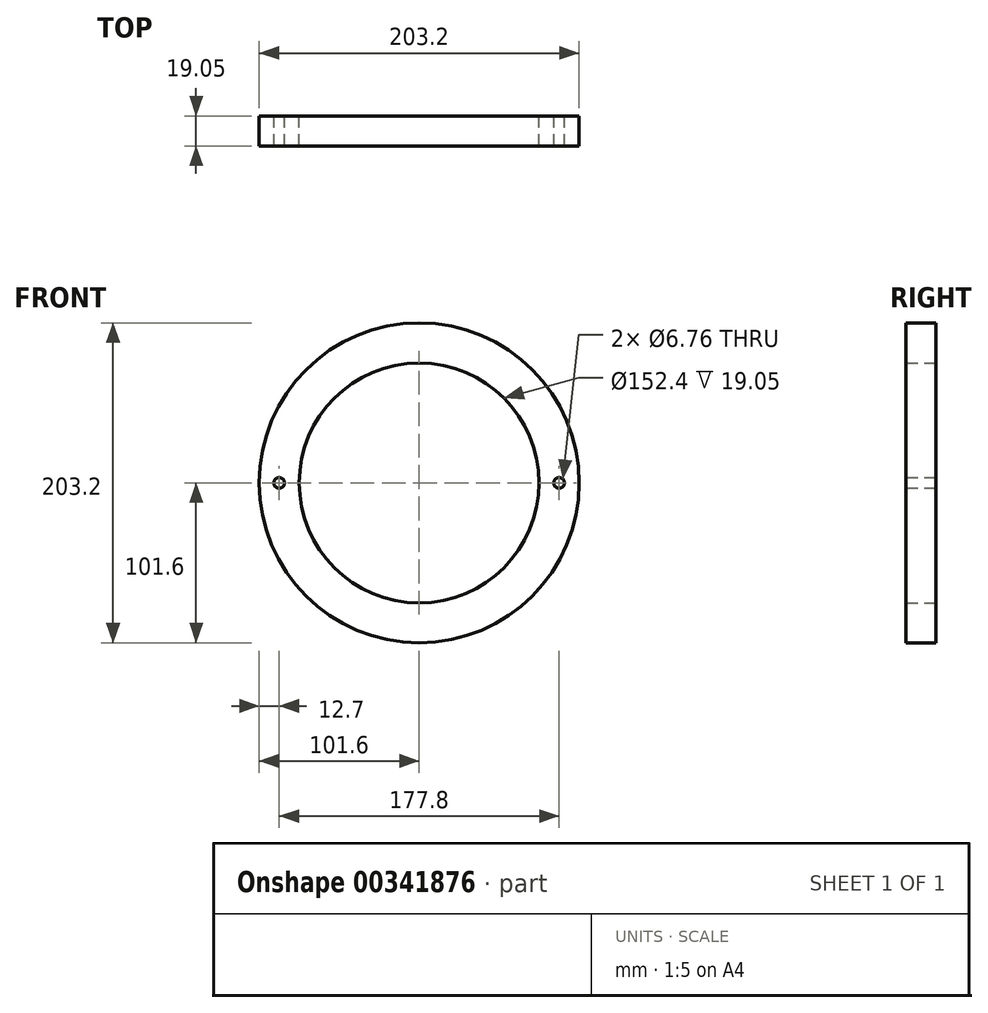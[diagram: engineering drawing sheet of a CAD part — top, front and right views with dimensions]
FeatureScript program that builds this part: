
annotation { "Feature Type Name" : "Feature", "Feature Type Description" : "" }
export const myFeature = defineFeature(function(context is Context, id is Id, definition is map)
    precondition{}
    {
        {
            var Q0;
            Q0=qCreatedBy(makeId("Front.planeOp"),FACE);
            var sketch = newSketch(context, id + "F0", { "sketchPlane" : qUnion([Q0])});
            skCircle(sketch, "E0", {"center": v(0, 0) * mm, "radius": 101.6 * mm});
            skCircle(sketch, "E1.0", {"center": v(0, 0) * mm, "radius": 76.2 * mm});
            skSolve(sketch);
        }
        {
            var Q0;
            Q0 = qSketchRegion(id + "F0", true);
            extrude(context, id + "F1", {"entities" : qUnion([Q0]), "depth" : 19.05 * mm});
        }
        {
            var Q0;
            Q0=makeQuery(id+"F1.opExtrude","CAP_FACE",FACE,{"disambiguationData":[OSD([sQuery(id+"F0.wireOp",EDGE,"E0"),sQuery(id+"F0.wireOp",EDGE,"E1.0")])],"isStart":false});
            var sketch = newSketch(context, id + "F2", { "sketchPlane" : qUnion([Q0])});
            skLineSegment(sketch, "E2", {"start": v(-101.6, 0) * mm, "end": v(-76.2, 0) * mm});
            skLineSegment(sketch, "E3", {"start": v(76.2, 0) * mm, "end": v(101.6, 0) * mm});
            skPoint(sketch, "E4", {"position": v(-88.9, 0) * mm});
            skPoint(sketch, "E5", {"position": v(88.9, 0) * mm});
            skSolve(sketch);
        }
        {
            var Q0;
            Q0=sQuery(id+"F2.wireOp",VERTEX,"E4");
            var Q1;
            Q1=sQuery(id+"F2.wireOp",VERTEX,"E5");
            var Q2;
            Q2=makeQuery(id+"F1.opExtrude","SWEPT_BODY",BODY,{"disambiguationData":[OSD([sQuery(id+"F0.wireOp",EDGE,"E0"),sQuery(id+"F0.wireOp",EDGE,"E1.0")])]});
            hole(context, id + "F3", {"style" : HoleStyle.SIMPLE, "endStyle" : HoleEndStyle.THROUGH, "standardTappedOrClearance" : lookupTablePath({ "standard" : "ANSI", "fit" : "Normal (ASME)", "size" : "1/4", "type" : "Clearance" }), "standardBlindInLast" : lookupTablePath({ "fit" : "Free", "standard" : "ANSI", "size" : "1/4", "type" : "Clearance" }), "holeDiameter" : 6.76 * mm, "isTappedThrough" : true, "tappedDepth" : 12.7 * mm, "tapClearance" : 3, "locations" : qUnion([Q0, Q1]), "scope" : qUnion([Q2])});
        }
    });
